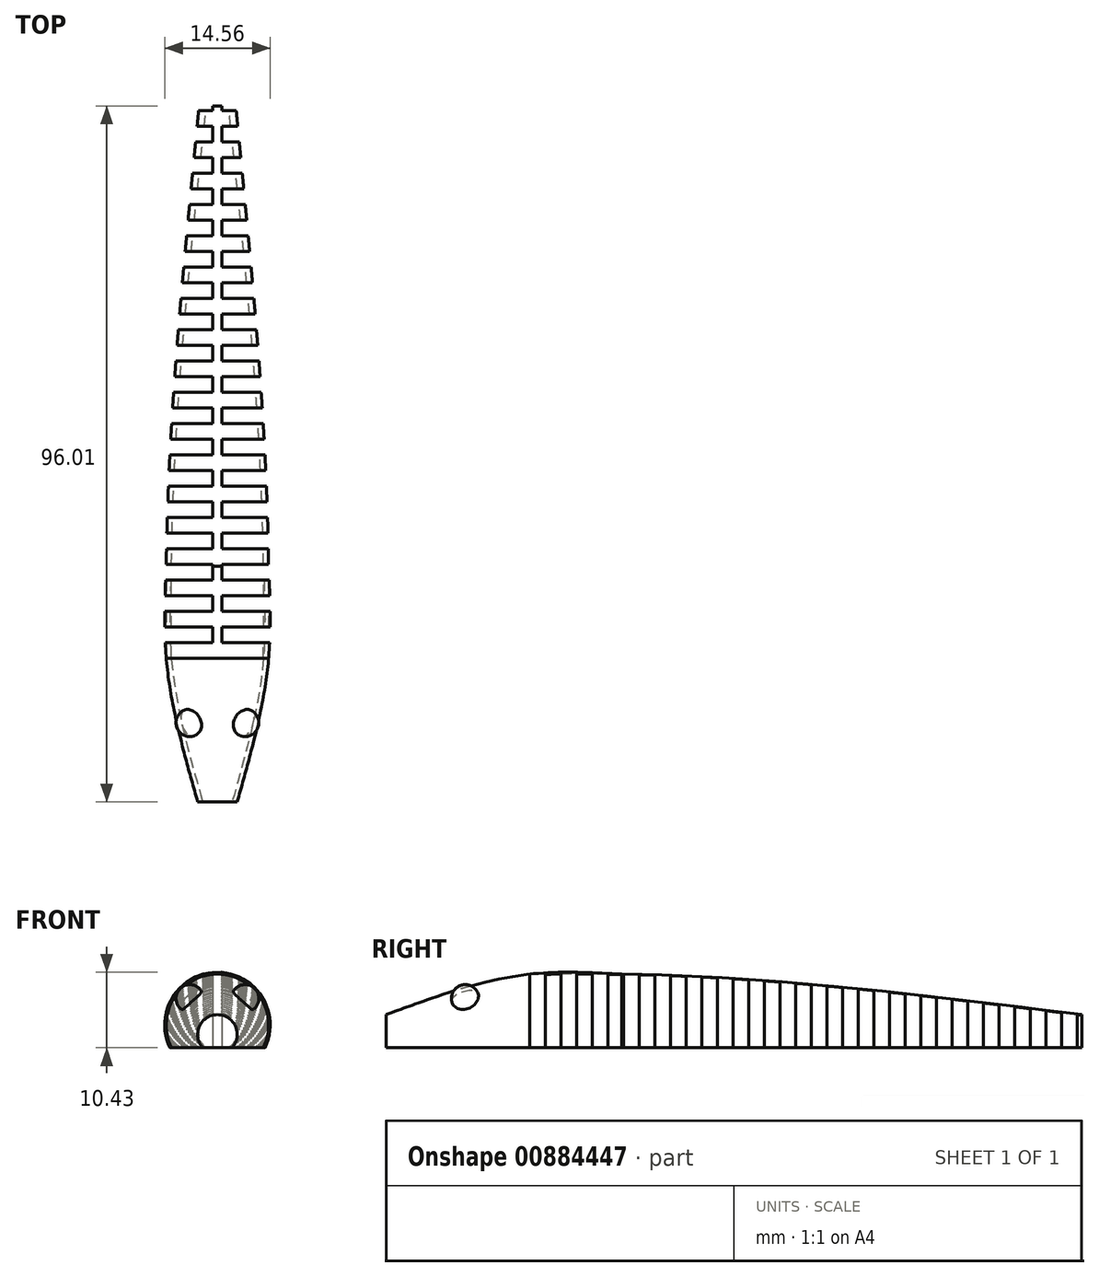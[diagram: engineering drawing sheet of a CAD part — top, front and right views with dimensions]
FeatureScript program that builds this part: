
annotation { "Feature Type Name" : "Feature", "Feature Type Description" : "" }
export const myFeature = defineFeature(function(context is Context, id is Id, definition is map)
    precondition{}
    {
        {
            var Q0;
            Q0=qCreatedBy(makeId("Front.planeOp"),FACE);
            var sketch = newSketch(context, id + "F0", { "sketchPlane" : qUnion([Q0])});
            skArc(sketch, "E0", {"start": v(6.35, 0) * mm, "mid": v(0, 10.16) * mm, "end": v(-6.35, 0) * mm});
            skPoint(sketch, "E0.first.point", {"position": v(-6.35, 0) * mm});
            skPoint(sketch, "E0.second.point", {"position": v(6.35, 0) * mm});
            skPoint(sketch, "E0.third.point", {"position": v(0, 10.16) * mm});
            skLineSegment(sketch, "E1", {"start": v(-6.35, 0) * mm, "end": v(6.35, 0) * mm});
            skSolve(sketch);
        }
        {
            var Q0;
            Q0=qCreatedBy(makeId("Front.planeOp"),FACE);
            cPlane(context, id + "F1", {"entities" : qUnion([Q0]), "cplaneType" : CPlaneType.OFFSET, "offset" : 12.7 * mm, "oppositeDirection" : true, "width" : 152.4 * mm, "height" : 152.4 * mm});
        }
        {
            var Q0;
            Q0=qCreatedBy(id+"F1.planeOp",FACE);
            var sketch = newSketch(context, id + "F2", { "sketchPlane" : qUnion([Q0])});
            skArc(sketch, "E2.0", {"start": v(6.35, 0) * mm, "mid": v(0, 10.16) * mm, "end": v(-6.35, 0) * mm});
            skLineSegment(sketch, "E2.1", {"start": v(-6.35, 0) * mm, "end": v(6.35, 0) * mm});
            skSolve(sketch);
        }
        {
            var Q0;
            Q0=qCreatedBy(id+"F1.planeOp",FACE);
            cPlane(context, id + "F3", {"entities" : qUnion([Q0]), "cplaneType" : CPlaneType.OFFSET, "offset" : 63.5 * mm, "oppositeDirection" : true, "width" : 152.4 * mm, "height" : 152.4 * mm});
        }
        {
            var Q0;
            Q0=qCreatedBy(id+"F3.planeOp",FACE);
            var sketch = newSketch(context, id + "F4", { "sketchPlane" : qUnion([Q0])});
            skPoint(sketch, "E3.0", {"position": v(0, 10.16) * mm});
            skPoint(sketch, "E4.0", {"position": v(6.35, 0) * mm});
            skPoint(sketch, "E5.0", {"position": v(-6.35, 0) * mm});
            skArc(sketch, "E6", {"start": v(1.52, 0) * mm, "mid": v(0, 4.57) * mm, "end": v(-1.52, 0) * mm});
            skPoint(sketch, "E6.first.point", {"position": v(1.52, 0) * mm});
            skPoint(sketch, "E6.second.point", {"position": v(-1.52, 0) * mm});
            skPoint(sketch, "E6.third.point", {"position": v(0, 4.57) * mm});
            skLineSegment(sketch, "E7", {"start": v(1.52, 0) * mm, "end": v(-1.52, 0) * mm});
            skSolve(sketch);
        }
        {
            var Q0;
            Q0=qCreatedBy(makeId("Front.planeOp"),FACE);
            cPlane(context, id + "F5", {"entities" : qUnion([Q0]), "cplaneType" : CPlaneType.OFFSET, "offset" : 19.8 * mm, "width" : 152.4 * mm, "height" : 152.4 * mm});
        }
        {
            var Q0;
            Q0=qCreatedBy(id+"F5.planeOp",FACE);
            var sketch = newSketch(context, id + "F6", { "sketchPlane" : qUnion([Q0])});
            skArc(sketch, "E8", {"start": v(2.03, 0) * mm, "mid": v(0, 4.57) * mm, "end": v(-2.03, 0) * mm});
            skPoint(sketch, "E8.first.point", {"position": v(-2.03, 0) * mm});
            skPoint(sketch, "E8.second.point", {"position": v(2.03, 0) * mm});
            skPoint(sketch, "E8.third.point", {"position": v(0, 4.57) * mm});
            skLineSegment(sketch, "E9", {"start": v(-2.03, 0) * mm, "end": v(2.03, 0) * mm});
            skSolve(sketch);
        }
        {
            var Q0;
            Q0=makeQuery(id+"F0.imprint","IMPRINT",FACE,{"disambiguationData":[TD([[makeQuery(id+"F0.imprint","IMPRINT",EDGE,{"derivedFrom":sQuery(id+"F0.wireOp",EDGE,"E0")}),1.0]])]});
            var Q1;
            Q1=makeQuery(id+"F2.imprint","IMPRINT",FACE,{"disambiguationData":[TD([[makeQuery(id+"F2.imprint","IMPRINT",EDGE,{"derivedFrom":sQuery(id+"F2.wireOp",EDGE,"E2.0")}),1.0]])]});
            var Q2;
            Q2=makeQuery(id+"F4.imprint","IMPRINT",FACE,{"disambiguationData":[TD([[makeQuery(id+"F4.imprint","IMPRINT",EDGE,{"derivedFrom":sQuery(id+"F4.wireOp",EDGE,"E6")}),1.0]])]});
            loft(context, id + "F7", {"sheetProfilesArray" : [{ "sheetProfileEntities" : qUnion([Q0]) }, { "sheetProfileEntities" : qUnion([Q1]) }, { "sheetProfileEntities" : qUnion([Q2]) }]});
        }
        {
            var Q0;
            Q0=qSketchRegion(id+"F2",true);
            var Q1;
            Q1=qSketchRegion(id+"F0",true);
            var Q2;
            Q2=qSketchRegion(id+"F6",true);
            loft(context, id + "F8", {"sheetProfilesArray" : [{ "sheetProfileEntities" : qUnion([Q0]) }, { "sheetProfileEntities" : qUnion([Q1]) }, { "sheetProfileEntities" : qUnion([Q2]) }]});
        }
        {
            var Q0;
            Q0=qCreatedBy(makeId("Top.planeOp"),FACE);
            var sketch = newSketch(context, id + "F9", { "sketchPlane" : qUnion([Q0])});
            skLineSegment(sketch, "E10.bottom", {"start": v(-9.53, 2.16) * mm, "end": v(-0.64, 2.16) * mm});
            skLineSegment(sketch, "E10.top", {"start": v(-9.53, 4.32) * mm, "end": v(-0.64, 4.32) * mm});
            skLineSegment(sketch, "E10.left", {"start": v(-9.53, 2.16) * mm, "end": v(-9.53, 4.32) * mm});
            skLineSegment(sketch, "E10.right", {"start": v(-0.64, 2.16) * mm, "end": v(-0.64, 4.32) * mm});
            skLineSegment(sketch, "E11", {"start": v(0, -25.2) * mm, "end": v(0, 80.38) * mm, "construction": true});
            skLineSegment(sketch, "E12.0.1.0", {"start": v(-9.53, 6.48) * mm, "end": v(-9.53, 8.64) * mm});
            skLineSegment(sketch, "E12.0.1.1", {"start": v(-0.64, 6.48) * mm, "end": v(-0.64, 8.64) * mm});
            skLineSegment(sketch, "E12.0.1.2", {"start": v(-9.53, 8.64) * mm, "end": v(-0.64, 8.64) * mm});
            skLineSegment(sketch, "E12.0.1.3", {"start": v(-9.53, 6.48) * mm, "end": v(-0.64, 6.48) * mm});
            skLineSegment(sketch, "E12.0.2.0", {"start": v(-9.53, 10.8) * mm, "end": v(-9.53, 12.95) * mm});
            skLineSegment(sketch, "E12.0.2.1", {"start": v(-0.64, 10.8) * mm, "end": v(-0.64, 12.95) * mm});
            skLineSegment(sketch, "E12.0.2.2", {"start": v(-9.53, 12.95) * mm, "end": v(-0.64, 12.95) * mm});
            skLineSegment(sketch, "E12.0.2.3", {"start": v(-9.53, 10.8) * mm, "end": v(-0.64, 10.8) * mm});
            skLineSegment(sketch, "E12.0.3.0", {"start": v(-9.53, 15.11) * mm, "end": v(-9.53, 17.27) * mm});
            skLineSegment(sketch, "E12.0.3.1", {"start": v(-0.64, 15.11) * mm, "end": v(-0.64, 17.27) * mm});
            skLineSegment(sketch, "E12.0.3.2", {"start": v(-9.53, 17.27) * mm, "end": v(-0.64, 17.27) * mm});
            skLineSegment(sketch, "E12.0.3.3", {"start": v(-9.53, 15.11) * mm, "end": v(-0.64, 15.11) * mm});
            skLineSegment(sketch, "E12.0.4.0", {"start": v(-9.53, 19.43) * mm, "end": v(-9.53, 21.6) * mm});
            skLineSegment(sketch, "E12.0.4.1", {"start": v(-0.64, 19.43) * mm, "end": v(-0.64, 21.59) * mm});
            skLineSegment(sketch, "E12.0.4.2", {"start": v(-9.53, 21.6) * mm, "end": v(-0.64, 21.6) * mm});
            skLineSegment(sketch, "E12.0.4.3", {"start": v(-9.53, 19.43) * mm, "end": v(-0.64, 19.43) * mm});
            skLineSegment(sketch, "E12.0.5.0", {"start": v(-9.53, 23.75) * mm, "end": v(-9.53, 25.9) * mm});
            skLineSegment(sketch, "E12.0.5.1", {"start": v(-0.64, 23.75) * mm, "end": v(-0.64, 25.9) * mm});
            skLineSegment(sketch, "E12.0.5.2", {"start": v(-9.53, 25.9) * mm, "end": v(-0.64, 25.9) * mm});
            skLineSegment(sketch, "E12.0.5.3", {"start": v(-9.53, 23.75) * mm, "end": v(-0.64, 23.75) * mm});
            skLineSegment(sketch, "E12.0.6.0", {"start": v(-9.53, 28.07) * mm, "end": v(-9.53, 30.23) * mm});
            skLineSegment(sketch, "E12.0.6.1", {"start": v(-0.64, 28.07) * mm, "end": v(-0.64, 30.23) * mm});
            skLineSegment(sketch, "E12.0.6.2", {"start": v(-9.53, 30.23) * mm, "end": v(-0.64, 30.23) * mm});
            skLineSegment(sketch, "E12.0.6.3", {"start": v(-9.53, 28.07) * mm, "end": v(-0.64, 28.07) * mm});
            skLineSegment(sketch, "E12.0.7.0", {"start": v(-9.53, 32.39) * mm, "end": v(-9.53, 34.54) * mm});
            skLineSegment(sketch, "E12.0.7.1", {"start": v(-0.64, 32.39) * mm, "end": v(-0.64, 34.54) * mm});
            skLineSegment(sketch, "E12.0.7.2", {"start": v(-9.53, 34.54) * mm, "end": v(-0.64, 34.54) * mm});
            skLineSegment(sketch, "E12.0.7.3", {"start": v(-9.53, 32.39) * mm, "end": v(-0.64, 32.39) * mm});
            skLineSegment(sketch, "E12.0.8.0", {"start": v(-9.53, 36.7) * mm, "end": v(-9.53, 38.86) * mm});
            skLineSegment(sketch, "E12.0.8.1", {"start": v(-0.64, 36.7) * mm, "end": v(-0.64, 38.86) * mm});
            skLineSegment(sketch, "E12.0.8.2", {"start": v(-9.53, 38.86) * mm, "end": v(-0.64, 38.86) * mm});
            skLineSegment(sketch, "E12.0.8.3", {"start": v(-9.53, 36.7) * mm, "end": v(-0.64, 36.7) * mm});
            skLineSegment(sketch, "E12.0.9.0", {"start": v(-9.53, 41.02) * mm, "end": v(-9.53, 43.18) * mm});
            skLineSegment(sketch, "E12.0.9.1", {"start": v(-0.64, 41.02) * mm, "end": v(-0.64, 43.18) * mm});
            skLineSegment(sketch, "E12.0.9.2", {"start": v(-9.53, 43.18) * mm, "end": v(-0.64, 43.18) * mm});
            skLineSegment(sketch, "E12.0.9.3", {"start": v(-9.53, 41.02) * mm, "end": v(-0.64, 41.02) * mm});
            skLineSegment(sketch, "E12.0.10.0", {"start": v(-9.53, 45.34) * mm, "end": v(-9.53, 47.5) * mm});
            skLineSegment(sketch, "E12.0.10.1", {"start": v(-0.64, 45.34) * mm, "end": v(-0.64, 47.5) * mm});
            skLineSegment(sketch, "E12.0.10.2", {"start": v(-9.53, 47.5) * mm, "end": v(-0.64, 47.5) * mm});
            skLineSegment(sketch, "E12.0.10.3", {"start": v(-9.53, 45.34) * mm, "end": v(-0.64, 45.34) * mm});
            skLineSegment(sketch, "E12.0.11.0", {"start": v(-9.53, 49.66) * mm, "end": v(-9.53, 51.82) * mm});
            skLineSegment(sketch, "E12.0.11.1", {"start": v(-0.64, 49.66) * mm, "end": v(-0.64, 51.82) * mm});
            skLineSegment(sketch, "E12.0.11.2", {"start": v(-9.53, 51.82) * mm, "end": v(-0.64, 51.82) * mm});
            skLineSegment(sketch, "E12.0.11.3", {"start": v(-9.53, 49.66) * mm, "end": v(-0.64, 49.66) * mm});
            skLineSegment(sketch, "E12.0.12.0", {"start": v(-9.53, 53.98) * mm, "end": v(-9.53, 56.13) * mm});
            skLineSegment(sketch, "E12.0.12.1", {"start": v(-0.64, 53.98) * mm, "end": v(-0.64, 56.13) * mm});
            skLineSegment(sketch, "E12.0.12.2", {"start": v(-9.53, 56.13) * mm, "end": v(-0.64, 56.13) * mm});
            skLineSegment(sketch, "E12.0.12.3", {"start": v(-9.53, 53.98) * mm, "end": v(-0.64, 53.98) * mm});
            skLineSegment(sketch, "E12.0.13.0", {"start": v(-9.53, 58.3) * mm, "end": v(-9.53, 60.45) * mm});
            skLineSegment(sketch, "E12.0.13.1", {"start": v(-0.64, 58.3) * mm, "end": v(-0.64, 60.45) * mm});
            skLineSegment(sketch, "E12.0.13.2", {"start": v(-9.53, 60.45) * mm, "end": v(-0.64, 60.45) * mm});
            skLineSegment(sketch, "E12.0.13.3", {"start": v(-9.53, 58.3) * mm, "end": v(-0.64, 58.3) * mm});
            skLineSegment(sketch, "E12.0.14.0", {"start": v(-9.53, 62.61) * mm, "end": v(-9.53, 64.77) * mm});
            skLineSegment(sketch, "E12.0.14.1", {"start": v(-0.64, 62.61) * mm, "end": v(-0.64, 64.77) * mm});
            skLineSegment(sketch, "E12.0.14.2", {"start": v(-9.53, 64.77) * mm, "end": v(-0.64, 64.77) * mm});
            skLineSegment(sketch, "E12.0.14.3", {"start": v(-9.53, 62.61) * mm, "end": v(-0.64, 62.61) * mm});
            skLineSegment(sketch, "E12.0.15.0", {"start": v(-9.53, 66.93) * mm, "end": v(-9.53, 69.09) * mm});
            skLineSegment(sketch, "E12.0.15.1", {"start": v(-0.64, 66.93) * mm, "end": v(-0.64, 69.09) * mm});
            skLineSegment(sketch, "E12.0.15.2", {"start": v(-9.53, 69.09) * mm, "end": v(-0.64, 69.09) * mm});
            skLineSegment(sketch, "E12.0.15.3", {"start": v(-9.53, 66.93) * mm, "end": v(-0.64, 66.93) * mm});
            skLineSegment(sketch, "E12.0.16.0", {"start": v(-9.53, 71.25) * mm, "end": v(-9.53, 73.4) * mm});
            skLineSegment(sketch, "E12.0.16.1", {"start": v(-0.64, 71.25) * mm, "end": v(-0.64, 73.4) * mm});
            skLineSegment(sketch, "E12.0.16.2", {"start": v(-9.53, 73.4) * mm, "end": v(-0.64, 73.4) * mm});
            skLineSegment(sketch, "E12.0.16.3", {"start": v(-9.53, 71.25) * mm, "end": v(-0.64, 71.25) * mm});
            skLineSegment(sketch, "E12.0.17.0", {"start": v(-9.53, 75.57) * mm, "end": v(-9.53, 77.72) * mm});
            skLineSegment(sketch, "E12.0.17.1", {"start": v(-0.64, 75.57) * mm, "end": v(-0.64, 77.72) * mm});
            skLineSegment(sketch, "E12.0.17.2", {"start": v(-9.53, 77.72) * mm, "end": v(-0.64, 77.72) * mm});
            skLineSegment(sketch, "E12.0.17.3", {"start": v(-9.53, 75.57) * mm, "end": v(-0.64, 75.57) * mm});
            skLineSegment(sketch, "E12.direction1", {"start": v(-9.52, 2.16) * mm, "end": v(15.88, 2.16) * mm, "construction": true});
            skLineSegment(sketch, "E12.direction2", {"start": v(-9.53, 2.16) * mm, "end": v(-9.53, 6.48) * mm, "construction": true});
            skLineSegment(sketch, "E13.MirrorCS", {"start": v(9.53, 66.93) * mm, "end": v(9.53, 69.09) * mm});
            skLineSegment(sketch, "E14.MirrorCS", {"start": v(9.53, 41.02) * mm, "end": v(9.53, 43.18) * mm});
            skLineSegment(sketch, "E15.MirrorCS", {"start": v(0.64, 36.7) * mm, "end": v(0.64, 38.86) * mm});
            skLineSegment(sketch, "E16.MirrorCS", {"start": v(0.64, 75.57) * mm, "end": v(0.64, 77.72) * mm});
            skLineSegment(sketch, "E17.MirrorCS", {"start": v(9.53, 6.48) * mm, "end": v(9.53, 8.64) * mm});
            skLineSegment(sketch, "E18.MirrorCS", {"start": v(0.64, 62.61) * mm, "end": v(0.64, 64.77) * mm});
            skLineSegment(sketch, "E19.MirrorCS", {"start": v(0.64, 2.16) * mm, "end": v(0.64, 4.32) * mm});
            skLineSegment(sketch, "E20.MirrorCS", {"start": v(9.53, 36.7) * mm, "end": v(9.53, 38.86) * mm});
            skLineSegment(sketch, "E21.MirrorCS", {"start": v(9.53, 32.39) * mm, "end": v(9.53, 34.54) * mm});
            skLineSegment(sketch, "E22.MirrorCS", {"start": v(0.64, 41.02) * mm, "end": v(0.64, 43.18) * mm});
            skLineSegment(sketch, "E23.MirrorCS", {"start": v(9.53, 62.61) * mm, "end": v(9.53, 64.77) * mm});
            skLineSegment(sketch, "E24.MirrorCS", {"start": v(0.64, 32.39) * mm, "end": v(0.64, 34.54) * mm});
            skLineSegment(sketch, "E25.MirrorCS", {"start": v(9.53, 2.16) * mm, "end": v(9.53, 4.32) * mm});
            skLineSegment(sketch, "E26.MirrorCS", {"start": v(0.64, 10.8) * mm, "end": v(0.64, 12.95) * mm});
            skLineSegment(sketch, "E27.MirrorCS", {"start": v(9.53, 10.8) * mm, "end": v(9.53, 12.95) * mm});
            skLineSegment(sketch, "E28.MirrorCS", {"start": v(0.64, 66.93) * mm, "end": v(0.64, 69.09) * mm});
            skLineSegment(sketch, "E29.MirrorCS", {"start": v(0.64, 6.48) * mm, "end": v(0.64, 8.64) * mm});
            skLineSegment(sketch, "E30.MirrorCS", {"start": v(0.64, 71.25) * mm, "end": v(0.64, 73.4) * mm});
            skLineSegment(sketch, "E31.MirrorCS", {"start": v(9.53, 23.75) * mm, "end": v(9.53, 25.9) * mm});
            skLineSegment(sketch, "E32.MirrorCS", {"start": v(9.53, 19.43) * mm, "end": v(9.53, 21.6) * mm});
            skLineSegment(sketch, "E33.MirrorCS", {"start": v(9.53, 25.9) * mm, "end": v(0.64, 25.9) * mm});
            skLineSegment(sketch, "E34.MirrorCS", {"start": v(9.53, 41.02) * mm, "end": v(0.64, 41.02) * mm});
            skLineSegment(sketch, "E35.MirrorCS", {"start": v(9.53, 45.34) * mm, "end": v(0.64, 45.34) * mm});
            skLineSegment(sketch, "E36.MirrorCS", {"start": v(0.64, 45.34) * mm, "end": v(0.64, 47.5) * mm});
            skLineSegment(sketch, "E37.MirrorCS", {"start": v(9.53, 69.09) * mm, "end": v(0.64, 69.09) * mm});
            skLineSegment(sketch, "E38.MirrorCS", {"start": v(9.53, 58.3) * mm, "end": v(0.64, 58.3) * mm});
            skLineSegment(sketch, "E39.MirrorCS", {"start": v(9.53, 77.72) * mm, "end": v(0.64, 77.72) * mm});
            skLineSegment(sketch, "E40.MirrorCS", {"start": v(9.53, 21.6) * mm, "end": v(0.64, 21.6) * mm});
            skLineSegment(sketch, "E41.MirrorCS", {"start": v(9.53, 71.25) * mm, "end": v(9.53, 73.4) * mm});
            skLineSegment(sketch, "E42.MirrorCS", {"start": v(9.53, 66.93) * mm, "end": v(0.64, 66.93) * mm});
            skLineSegment(sketch, "E43.MirrorCS", {"start": v(9.53, 15.11) * mm, "end": v(0.64, 15.11) * mm});
            skLineSegment(sketch, "E44.MirrorCS", {"start": v(9.53, 62.61) * mm, "end": v(0.64, 62.61) * mm});
            skLineSegment(sketch, "E45.MirrorCS", {"start": v(0.64, 53.98) * mm, "end": v(0.64, 56.13) * mm});
            skLineSegment(sketch, "E46.MirrorCS", {"start": v(9.53, 75.57) * mm, "end": v(0.64, 75.57) * mm});
            skLineSegment(sketch, "E47.MirrorCS", {"start": v(0.64, 23.75) * mm, "end": v(0.64, 25.9) * mm});
            skLineSegment(sketch, "E48.MirrorCS", {"start": v(9.53, 15.11) * mm, "end": v(9.53, 17.27) * mm});
            skLineSegment(sketch, "E49.MirrorCS", {"start": v(9.53, 73.4) * mm, "end": v(0.64, 73.4) * mm});
            skLineSegment(sketch, "E50.MirrorCS", {"start": v(0.64, 28.07) * mm, "end": v(0.64, 30.23) * mm});
            skLineSegment(sketch, "E51.MirrorCS", {"start": v(9.53, 71.25) * mm, "end": v(0.64, 71.25) * mm});
            skLineSegment(sketch, "E52.MirrorCS", {"start": v(9.53, 49.66) * mm, "end": v(0.64, 49.66) * mm});
            skLineSegment(sketch, "E53.MirrorCS", {"start": v(9.53, 58.3) * mm, "end": v(9.53, 60.45) * mm});
            skLineSegment(sketch, "E54.MirrorCS", {"start": v(9.53, 51.82) * mm, "end": v(0.64, 51.82) * mm});
            skLineSegment(sketch, "E55.MirrorCS", {"start": v(9.53, 49.66) * mm, "end": v(9.53, 51.82) * mm});
            skLineSegment(sketch, "E56.MirrorCS", {"start": v(9.53, 12.95) * mm, "end": v(0.64, 12.95) * mm});
            skLineSegment(sketch, "E57.MirrorCS", {"start": v(9.53, 64.77) * mm, "end": v(0.64, 64.77) * mm});
            skLineSegment(sketch, "E58.MirrorCS", {"start": v(9.53, 28.07) * mm, "end": v(9.53, 30.23) * mm});
            skLineSegment(sketch, "E59.MirrorCS", {"start": v(9.53, 19.43) * mm, "end": v(0.64, 19.43) * mm});
            skLineSegment(sketch, "E60.MirrorCS", {"start": v(9.53, 45.34) * mm, "end": v(9.53, 47.5) * mm});
            skLineSegment(sketch, "E61.MirrorCS", {"start": v(9.53, 56.13) * mm, "end": v(0.64, 56.13) * mm});
            skLineSegment(sketch, "E62.MirrorCS", {"start": v(9.53, 28.07) * mm, "end": v(0.64, 28.07) * mm});
            skLineSegment(sketch, "E63.MirrorCS", {"start": v(9.53, 38.86) * mm, "end": v(0.64, 38.86) * mm});
            skLineSegment(sketch, "E64.MirrorCS", {"start": v(9.53, 47.5) * mm, "end": v(0.64, 47.5) * mm});
            skLineSegment(sketch, "E65.MirrorCS", {"start": v(0.64, 58.3) * mm, "end": v(0.64, 60.45) * mm});
            skLineSegment(sketch, "E66.MirrorCS", {"start": v(9.53, 8.64) * mm, "end": v(0.64, 8.64) * mm});
            skLineSegment(sketch, "E67.MirrorCS", {"start": v(9.53, 30.23) * mm, "end": v(0.64, 30.23) * mm});
            skLineSegment(sketch, "E68.MirrorCS", {"start": v(0.64, 49.66) * mm, "end": v(0.64, 51.82) * mm});
            skLineSegment(sketch, "E69.MirrorCS", {"start": v(9.53, 6.48) * mm, "end": v(0.64, 6.48) * mm});
            skLineSegment(sketch, "E70.MirrorCS", {"start": v(0.64, 19.43) * mm, "end": v(0.64, 21.59) * mm});
            skLineSegment(sketch, "E71.MirrorCS", {"start": v(9.53, 4.32) * mm, "end": v(0.64, 4.32) * mm});
            skLineSegment(sketch, "E72.MirrorCS", {"start": v(9.53, 23.75) * mm, "end": v(0.64, 23.75) * mm});
            skLineSegment(sketch, "E73.MirrorCS", {"start": v(9.53, 2.16) * mm, "end": v(9.53, 6.48) * mm, "construction": true});
            skLineSegment(sketch, "E74.MirrorCS", {"start": v(0.64, 15.11) * mm, "end": v(0.64, 17.27) * mm});
            skLineSegment(sketch, "E75.MirrorCS", {"start": v(9.53, 53.98) * mm, "end": v(0.64, 53.98) * mm});
            skLineSegment(sketch, "E76.MirrorCS", {"start": v(9.53, 75.57) * mm, "end": v(9.53, 77.72) * mm});
            skLineSegment(sketch, "E77.MirrorCS", {"start": v(9.53, 43.18) * mm, "end": v(0.64, 43.18) * mm});
            skLineSegment(sketch, "E78.MirrorCS", {"start": v(9.53, 2.16) * mm, "end": v(0.64, 2.16) * mm});
            skLineSegment(sketch, "E79.MirrorCS", {"start": v(9.53, 17.27) * mm, "end": v(0.64, 17.27) * mm});
            skLineSegment(sketch, "E80.MirrorCS", {"start": v(9.53, 10.8) * mm, "end": v(0.64, 10.8) * mm});
            skLineSegment(sketch, "E81.MirrorCS", {"start": v(9.53, 60.45) * mm, "end": v(0.64, 60.45) * mm});
            skLineSegment(sketch, "E82.MirrorCS", {"start": v(9.53, 34.54) * mm, "end": v(0.64, 34.54) * mm});
            skLineSegment(sketch, "E83.MirrorCS", {"start": v(9.53, 36.7) * mm, "end": v(0.64, 36.7) * mm});
            skLineSegment(sketch, "E84.MirrorCS", {"start": v(9.53, 32.39) * mm, "end": v(0.64, 32.39) * mm});
            skLineSegment(sketch, "E85.MirrorCS", {"start": v(9.53, 53.98) * mm, "end": v(9.53, 56.13) * mm});
            skSolve(sketch);
        }
        {
            var Q0;
            Q0=qSketchRegion(id+"F9",true);
            extrude(context, id + "F10", {"entities" : qUnion([Q0]), "operationType" : NewBodyOperationType.REMOVE, "endBound" : BoundingType.THROUGH_ALL, "depth" : 25.4 * mm, "offsetDistance" : 25.4 * mm});
        }
        {
            var Q0;
            Q0=qCreatedBy(makeId("Right.planeOp"),FACE);
            cPlane(context, id + "F11", {"entities" : qUnion([Q0]), "cplaneType" : CPlaneType.OFFSET, "offset" : 3.8 * mm, "width" : 152.4 * mm, "height" : 152.4 * mm});
        }
        {
            var Q0;
            Q0=qCreatedBy(id+"F11.planeOp",FACE);
            var sketch = newSketch(context, id + "F12", { "sketchPlane" : qUnion([Q0])});
            skFitSpline(sketch, "E86", {"points": [v(12.7, 9.04) * mm, v(10.8, 9.17) * mm, v(7.93, 9.34) * mm, v(4.1, 9.36) * mm, v(1.24, 9.22) * mm, v(-1.57, 8.85) * mm, v(-4.34, 8.26) * mm, v(-7.08, 7.47) * mm, v(-8.89, 6.83) * mm, v(-9.78, 6.48) * mm, v(-10.5, 6.18) * mm, v(-11.59, 5.72) * mm, v(-12.99, 5.01) * mm, v(-13.67, 4.62) * mm, v(-14, 4.4) * mm, v(-14.15, 4.31) * mm, v(-14.45, 4.11) * mm, v(-14.88, 3.79) * mm, v(-15.29, 3.43) * mm, v(-15.53, 3.16) * mm, v(-15.63, 3.02) * mm, v(-15.75, 2.86) * mm, v(-15.9, 2.6) * mm, v(-15.96, 2.21) * mm, v(-15.94, 2.02) * mm, v(-15.92, 1.93) * mm, v(-15.87, 1.73) * mm, v(-15.65, 1.37) * mm, v(-15.34, 1.09) * mm, v(-15.18, 0.96) * mm, v(-14.91, 0.76) * mm, v(-14.33, 0.41) * mm, v(-13.72, 0.13) * mm, v(-13.4, 0) * mm]});
            skFitSpline(sketch, "E87", {"points": [v(12.7, 9.04) * mm, v(10.8, 9.17) * mm, v(7.93, 9.34) * mm, v(4.1, 9.36) * mm, v(1.24, 9.22) * mm, v(-1.57, 8.85) * mm, v(-4.34, 8.26) * mm, v(-7.08, 7.47) * mm, v(-8.89, 6.83) * mm, v(-9.78, 6.48) * mm, v(-10.5, 6.18) * mm, v(-11.59, 5.72) * mm, v(-12.99, 5.01) * mm, v(-13.67, 4.62) * mm, v(-14, 4.4) * mm, v(-14.15, 4.31) * mm, v(-14.45, 4.11) * mm, v(-14.88, 3.79) * mm, v(-15.29, 3.43) * mm, v(-15.53, 3.16) * mm, v(-15.63, 3.02) * mm, v(-15.75, 2.86) * mm, v(-15.9, 2.6) * mm, v(-15.96, 2.21) * mm, v(-15.94, 2.02) * mm, v(-15.92, 1.93) * mm, v(-15.87, 1.73) * mm, v(-15.65, 1.37) * mm, v(-15.34, 1.09) * mm, v(-15.18, 0.96) * mm, v(-14.91, 0.76) * mm, v(-14.33, 0.41) * mm, v(-13.72, 0.13) * mm, v(-13.4, 0) * mm]});
            skFitSpline(sketch, "E88", {"points": [v(12.7, 9.04) * mm, v(10.8, 9.17) * mm, v(7.93, 9.34) * mm, v(4.1, 9.36) * mm, v(1.24, 9.22) * mm, v(-1.57, 8.85) * mm, v(-4.34, 8.26) * mm, v(-7.08, 7.47) * mm, v(-8.89, 6.83) * mm, v(-9.78, 6.48) * mm, v(-10.5, 6.18) * mm, v(-11.59, 5.72) * mm, v(-12.99, 5.01) * mm, v(-13.67, 4.62) * mm, v(-14, 4.4) * mm, v(-14.15, 4.31) * mm, v(-14.45, 4.11) * mm, v(-14.88, 3.79) * mm, v(-15.29, 3.43) * mm, v(-15.53, 3.16) * mm, v(-15.63, 3.02) * mm, v(-15.75, 2.86) * mm, v(-15.9, 2.6) * mm, v(-15.96, 2.21) * mm, v(-15.94, 2.02) * mm, v(-15.92, 1.93) * mm, v(-15.87, 1.73) * mm, v(-15.65, 1.37) * mm, v(-15.34, 1.09) * mm, v(-15.18, 0.96) * mm, v(-14.91, 0.76) * mm, v(-14.33, 0.41) * mm, v(-13.72, 0.13) * mm, v(-13.4, 0) * mm]});
            skPoint(sketch, "E89", {"position": v(-8.9, 6.82) * mm});
            skArc(sketch, "E90", {"start": v(-6.99, 6.82) * mm, "mid": v(-8.9, 8.72) * mm, "end": v(-10.8, 6.82) * mm});
            skLineSegment(sketch, "E91", {"start": v(-8.9, 6.82) * mm, "end": v(-6.99, 6.82) * mm});
            skLineSegment(sketch, "E92", {"start": v(-8.9, 6.82) * mm, "end": v(-10.8, 6.82) * mm});
            skFitSpline(sketch, "E93.trimOffspring", {"points": [v(12.7, 9.04) * mm, v(10.8, 9.17) * mm, v(7.93, 9.34) * mm, v(4.1, 9.36) * mm, v(1.24, 9.22) * mm, v(-1.57, 8.85) * mm, v(-4.34, 8.26) * mm, v(-7.08, 7.47) * mm, v(-8.89, 6.83) * mm, v(-9.78, 6.48) * mm, v(-10.5, 6.18) * mm, v(-11.59, 5.72) * mm, v(-12.99, 5.01) * mm, v(-13.67, 4.62) * mm, v(-14, 4.4) * mm, v(-14.15, 4.31) * mm, v(-14.45, 4.11) * mm, v(-14.88, 3.79) * mm, v(-15.29, 3.43) * mm, v(-15.53, 3.16) * mm, v(-15.63, 3.02) * mm, v(-15.75, 2.86) * mm, v(-15.9, 2.6) * mm, v(-15.96, 2.21) * mm, v(-15.94, 2.02) * mm, v(-15.92, 1.93) * mm, v(-15.87, 1.73) * mm, v(-15.65, 1.37) * mm, v(-15.34, 1.09) * mm, v(-15.18, 0.96) * mm, v(-14.91, 0.76) * mm, v(-14.33, 0.41) * mm, v(-13.72, 0.13) * mm, v(-13.4, 0) * mm]});
            skSolve(sketch);
        }
        {
            var Q0;
            Q0=qSketchRegion(id+"F12",true);
            var Q1;
            Q1=sQuery(id+"F12.wireOp",EDGE,"E92");
            revolve(context, id + "F13", {"surfaceOperationType" : NewSurfaceOperationType.NEW, "entities" : qUnion([Q0]), "axis" : qUnion([Q1]), "revolveType" : RevolveType.FULL});
        }
        {
            var Q0;
            Q0=makeQuery(id+"F13.opRevolve","SWEPT_BODY",BODY,{"disambiguationData":[OSD([sQuery(id+"F12.wireOp",EDGE,"E90"),sQuery(id+"F12.wireOp",EDGE,"E91"),sQuery(id+"F12.wireOp",EDGE,"E92")])]});
            var Q1;
            Q1=qCreatedBy(makeId("Right.planeOp"),FACE);
            mirror(context, id + "F14", {"operationType" : NewBodyOperationType.ADD, "entities" : qUnion([Q0]), "mirrorPlane" : qUnion([Q1])});
        }
    });
